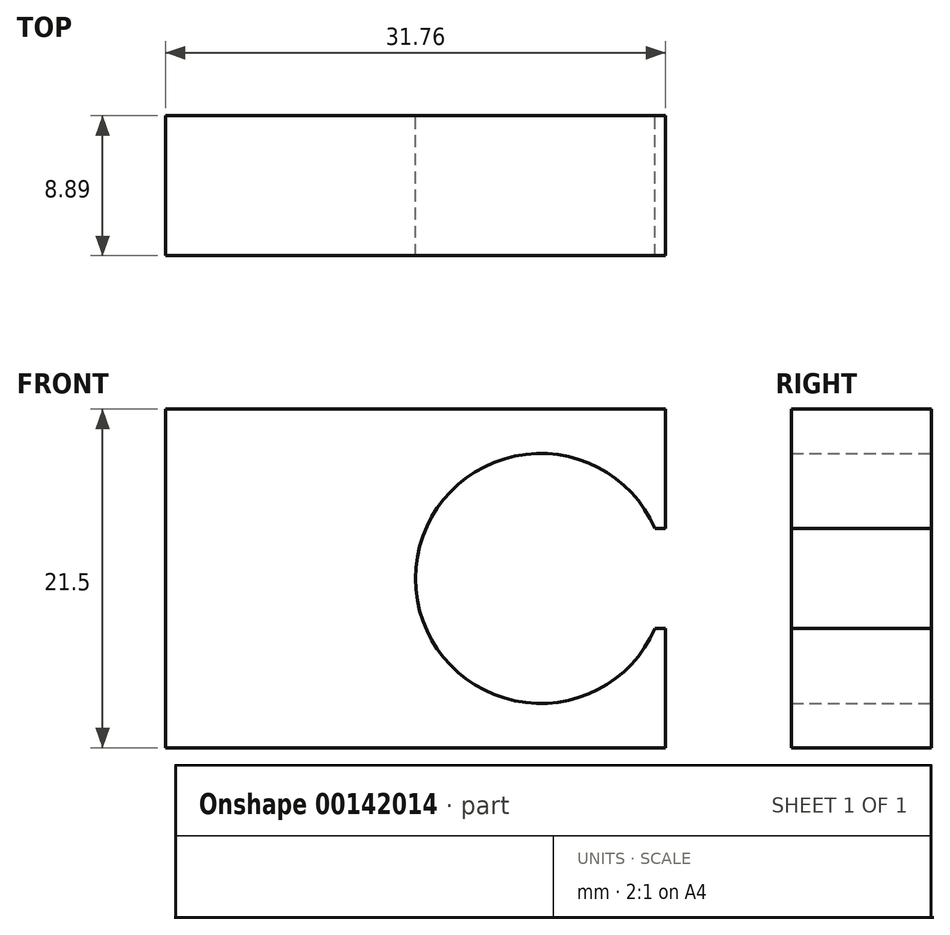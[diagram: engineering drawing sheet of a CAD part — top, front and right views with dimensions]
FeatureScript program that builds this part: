
annotation { "Feature Type Name" : "Feature", "Feature Type Description" : "" }
export const myFeature = defineFeature(function(context is Context, id is Id, definition is map)
    precondition{}
    {
        {
            var Q0;
            Q0=qCreatedBy(makeId("Front.planeOp"),FACE);
            var sketch = newSketch(context, id + "F0", { "sketchPlane" : qUnion([Q0])});
            skLineSegment(sketch, "E0.bottom", {"start": v(15.88, 10.75) * mm, "end": v(-15.88, 10.75) * mm});
            skLineSegment(sketch, "E0.top", {"start": v(15.87, -10.75) * mm, "end": v(-15.87, -10.75) * mm});
            skLineSegment(sketch, "E0.left", {"start": v(15.88, 10.75) * mm, "end": v(15.88, 3.17) * mm});
            skLineSegment(sketch, "E0.right", {"start": v(-15.88, 10.75) * mm, "end": v(-15.88, -10.75) * mm});
            skPoint(sketch, "E0.middle", {"position": v(0, 0) * mm});
            skArc(sketch, "E1", {"start": v(15.21, 3.18) * mm, "mid": v(0, 0) * mm, "end": v(15.21, -3.18) * mm});
            skLineSegment(sketch, "E2", {"start": v(15.21, 3.17) * mm, "end": v(15.88, 3.17) * mm});
            skLineSegment(sketch, "E3", {"start": v(0, 0) * mm, "end": v(15.88, 0) * mm, "construction": true});
            skLineSegment(sketch, "E4.MirrorCS", {"start": v(15.21, -3.18) * mm, "end": v(15.88, -3.18) * mm});
            skLineSegment(sketch, "E5.trimOffspring", {"start": v(15.88, -3.18) * mm, "end": v(15.88, -10.75) * mm});
            skSolve(sketch);
        }
        {
            var Q0;
            Q0=makeQuery(id+"F0.imprint","IMPRINT",FACE,{"disambiguationData":[TD([[makeQuery(id+"F0.imprint","IMPRINT",EDGE,{"derivedFrom":sQuery(id+"F0.wireOp",EDGE,"E0.bottom")}),1.0]])]});
            extrude(context, id + "F1", {"entities" : qUnion([Q0]), "depth" : 8.9 * mm});
        }
    });
